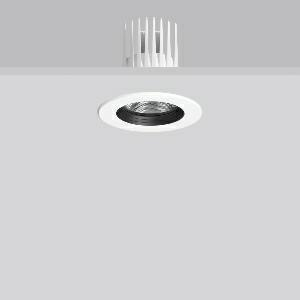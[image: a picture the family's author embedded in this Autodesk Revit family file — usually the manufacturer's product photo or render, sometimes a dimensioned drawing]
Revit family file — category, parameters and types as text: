
# Revit family: heledon_mini_e_901742_002_2_edac
name_source: partatom
category: Lighting Fixtures
units: mm (PartAtom-declared; Revit-internal decimal feet)

## family parameters
Cut with Voids When Loaded = No
Host = Face
Light Source = No
Part Type = Normal
Room Calculation Point = No
Round Connector Dimension = Use Diameter
Shared = No

## types (1)
- HELEDON mini E (1 x LED Modul 927, 2400 lm, 2700)
    Apparent Load = 20 VA
    Approval mark = CE
    CIE Flux Codes = 95 99 100 100 100
    Color Rendering = 92
    Color Temperature = 2700
    Default Elevation = 1800 mm
    Description = Series: HELEDON mini
Round recessed downlight. Housing: die-cast aluminium, powder-coated. Black plastic ring and recessed LED to prevent glare from the side. Optical assembly with reflector made of MIRO-Silver with 98% total light reflection for outstanding efficiency - can be changed without tools. Best colour rendering index Ra>90. Suitable for Recessed ceiling mounting. Installation without tools thanks to spring fastening system. Including separate LED converter with connecting cable 600 mm.High quality converter without flickering and stroboscopic effect. Through-wiring box (5 pole) available as accessory. The following accessories can be mounted without use of tools: interchangeable lenses, decorative glasses, honeycomb louvre, clear and frosted diffusers, white interchangeable plastic ring. 
Colour: traffic white, matt (RAL 9016)
Diameter: 124 mm
Height: 3 mm
Cut-out diameter: 114 mm
Recess height: 170 mm
Luminaire: recess height: 120 mm
Lamp: LED
Socket: without socket
Colour temperature: 2700K
Colour rendering index (CRI): 92
System power: 20 W
Rated luminous flux: 2400 lm
Luminous efficiency: 120 lm/W
Control gear: Regulated power supply
Protection class: II
Type of protection: IP 20
    Height = 0 mm  [stored 0 ft]
    Lamp = 1 x LED Modul 927
    Lamp Light Flux = 2400 lm
    Lamp count = 1
    Length = 124 mm  [stored 0.406824 ft]
    Lifetime = 50000 h
    Luminous efficacy = 120 lm/W
    Manufacturer = RZB
    ModVariant = No
    Model = 901742.002.2
    Mounting Place = Ceiling
    Mounting Type = Recessed
    Number of Poles = 1
    OnlyDefault = Yes
    Power Factor = 1
    Product Name = HELEDON mini E
    Product group = Recessed downlights
    ProductGroupID = 402
    Protection Class = Protection class II
    Protection Degree = IP 20
    RLX_Detail_Level = 1
    RLX_Emergency_Light_Flux = 0 lm
    RLX_Emergency_Type = 0
    RLX_Emergency_Type_DB = No
    RlxData = <blob elided: 126313 chars, md5=b0c3950b>
    Socket = socket
    Standby Power = 0 W
    System Light Flux = 2400 lm
    System Power = 20 W
    Type Comments = Product without accessories
    Type Image = 901657.002.jpg
    URL = http://relux.com
    VarID = ---
    Voltage = 230 V
    Voltage Range = 220-240 V
    Weight = 0.00 kg
    Width = 0 mm  [stored 0 ft]

note: [stored X ft] marks values corroborated as IEEE doubles in the binary element streams (Revit-internal decimal feet)

## geometry (parser evidence)
native form markers: Blend x4, Sweep x12
no freeform markers — native parametric forms only
